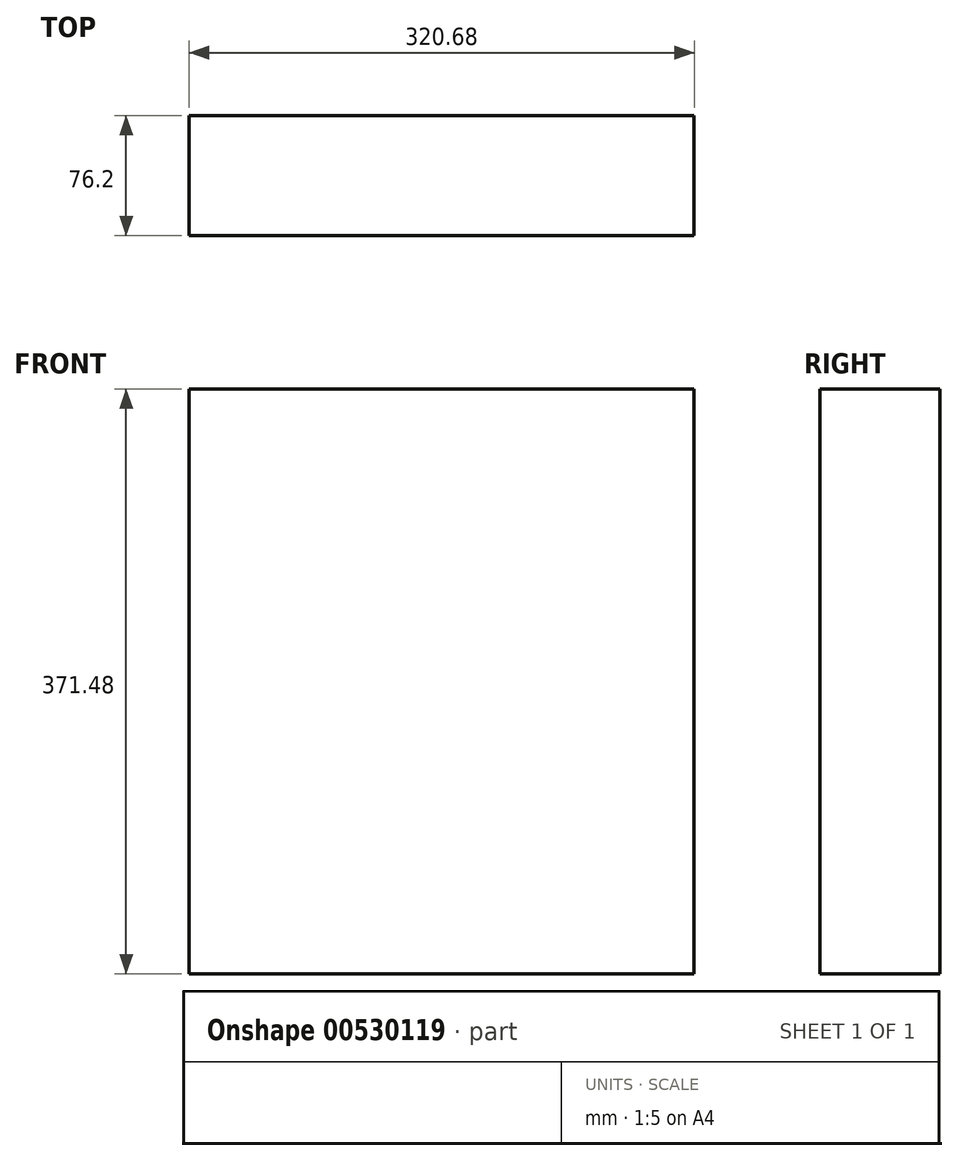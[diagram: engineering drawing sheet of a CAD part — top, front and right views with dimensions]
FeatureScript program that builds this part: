
annotation { "Feature Type Name" : "Feature", "Feature Type Description" : "" }
export const myFeature = defineFeature(function(context is Context, id is Id, definition is map)
    precondition{}
    {
        {
            var Q0;
            Q0=qCreatedBy(makeId("Front.planeOp"),FACE);
            var sketch = newSketch(context, id + "F0", { "sketchPlane" : qUnion([Q0])});
            skLineSegment(sketch, "E0.bottom", {"start": v(-160.34, -185.74) * mm, "end": v(160.34, -185.74) * mm});
            skLineSegment(sketch, "E0.top", {"start": v(-160.34, 185.74) * mm, "end": v(160.34, 185.74) * mm});
            skLineSegment(sketch, "E0.left", {"start": v(-160.34, -185.74) * mm, "end": v(-160.34, 185.74) * mm});
            skLineSegment(sketch, "E0.right", {"start": v(160.34, -185.74) * mm, "end": v(160.34, 185.74) * mm});
            skPoint(sketch, "E0.middle", {"position": v(0, 0) * mm});
            skSolve(sketch);
        }
        {
            var Q0;
            Q0 = qSketchRegion(id + "F0", true);
            extrude(context, id + "F1", {"entities" : qUnion([Q0]), "endBound" : BoundingType.SYMMETRIC, "depth" : 76.2 * mm, "offsetDistance" : 25.4 * mm});
        }
    });
